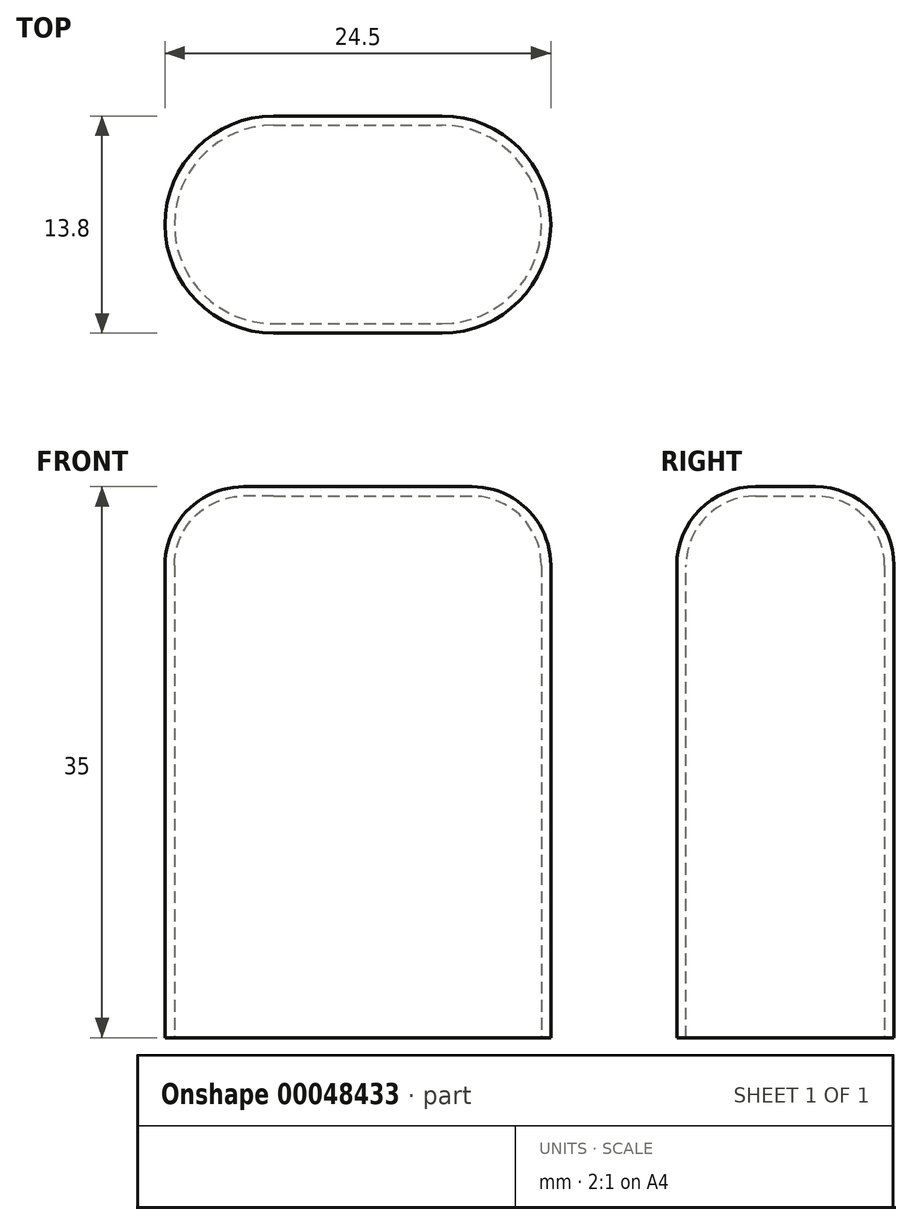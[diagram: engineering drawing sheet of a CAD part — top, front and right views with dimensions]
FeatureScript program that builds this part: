
annotation { "Feature Type Name" : "Feature", "Feature Type Description" : "" }
export const myFeature = defineFeature(function(context is Context, id is Id, definition is map)
    precondition{}
    {
        {
            var Q0;
            Q0=qCreatedBy(makeId("Top.planeOp"),FACE);
            var sketch = newSketch(context, id + "F0", { "sketchPlane" : qUnion([Q0])});
            skArc(sketch, "E0", {"start": v(-5.35, 6.9) * mm, "mid": v(-12.25, 0) * mm, "end": v(-5.35, -6.9) * mm});
            skArc(sketch, "E1.MirrorC", {"start": v(5.35, 6.9) * mm, "mid": v(12.25, 0) * mm, "end": v(5.35, -6.9) * mm});
            skLineSegment(sketch, "E2", {"start": v(-5.35, 6.9) * mm, "end": v(5.35, 6.9) * mm});
            skLineSegment(sketch, "E3.MirrorCS", {"start": v(-5.35, -6.9) * mm, "end": v(5.35, -6.9) * mm});
            skSolve(sketch);
        }
        {
            var Q0;
            Q0 = qSketchRegion(id + "F0", true);
            extrude(context, id + "F1", {"entities" : qUnion([Q0]), "depth" : 35 * mm});
        }
        {
            var Q0;
            Q0=makeQuery(id+"F1.opExtrude","CAP_EDGE",EDGE,{"disambiguationData":[OSD([sQuery(id+"F0.wireOp",EDGE,"E3.MirrorCS")])],"isStart":false});
            fillet(context, id + "F2", {"entities" : qUnion([Q0]), "radius" : 5 * mm, "tangentPropagation" : true, "allowEdgeOverflow" : false});
        }
        {
            var Q0;
            Q0=makeQuery(id+"F1.opExtrude","CAP_FACE",FACE,{"disambiguationData":[OSD([sQuery(id+"F0.wireOp",EDGE,"E0"),sQuery(id+"F0.wireOp",EDGE,"E1.MirrorC"),sQuery(id+"F0.wireOp",EDGE,"E2"),sQuery(id+"F0.wireOp",EDGE,"E3.MirrorCS")])],"isStart":true});
            shell(context, id + "F3", {"entities" : qUnion([Q0]), "thickness" : 0.6 * mm});
        }
    });
